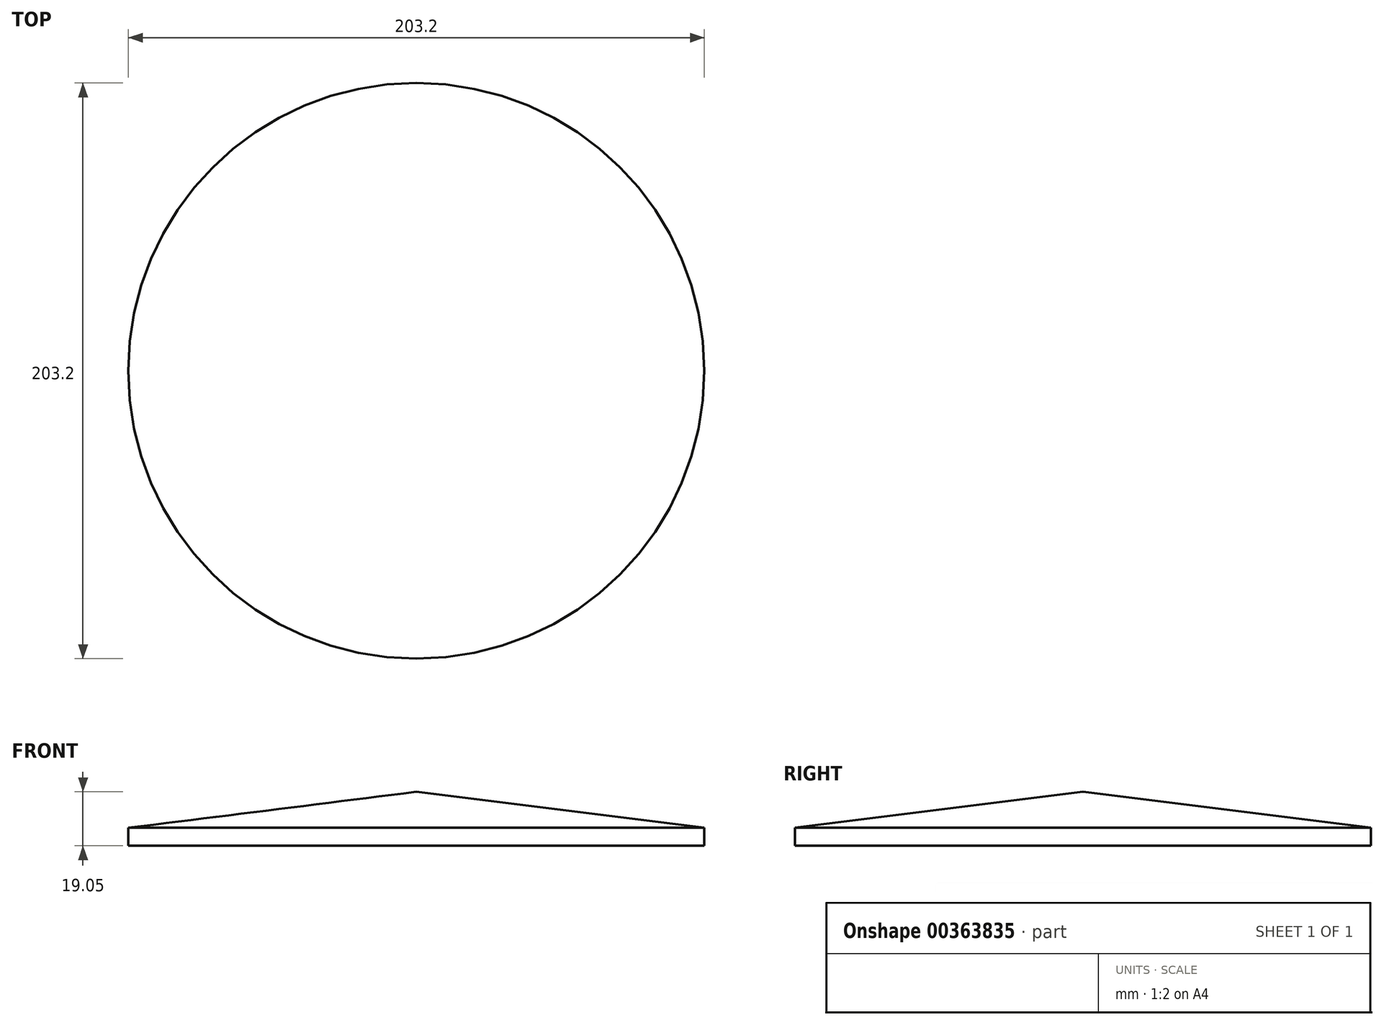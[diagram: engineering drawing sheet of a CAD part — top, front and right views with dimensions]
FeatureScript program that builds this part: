
annotation { "Feature Type Name" : "Feature", "Feature Type Description" : "" }
export const myFeature = defineFeature(function(context is Context, id is Id, definition is map)
    precondition{}
    {
        {
            var Q0;
            Q0=qCreatedBy(makeId("Front.planeOp"),FACE);
            var sketch = newSketch(context, id + "F0", { "sketchPlane" : qUnion([Q0])});
            skLineSegment(sketch, "E0.bottom", {"start": v(0, 0) * mm, "end": v(-101.6, 0) * mm});
            skLineSegment(sketch, "E0.top", {"start": v(0, 19.05) * mm, "end": v(-101.6, 19.05) * mm});
            skLineSegment(sketch, "E0.left", {"start": v(0, 0) * mm, "end": v(0, 19.05) * mm});
            skLineSegment(sketch, "E0.right", {"start": v(-101.6, 0) * mm, "end": v(-101.6, 19.05) * mm});
            skLineSegment(sketch, "E1", {"start": v(-101.6, 6.35) * mm, "end": v(0, 19.05) * mm});
            skLineSegment(sketch, "E2.bottom", {"start": v(0, 0) * mm, "end": v(-22.23, 0) * mm});
            skLineSegment(sketch, "E2.top", {"start": v(0, 152.4) * mm, "end": v(-22.23, 152.4) * mm});
            skLineSegment(sketch, "E2.left", {"start": v(0, 0) * mm, "end": v(0, 152.4) * mm});
            skLineSegment(sketch, "E2.right", {"start": v(-22.23, 0) * mm, "end": v(-22.23, 152.4) * mm});
            skLineSegment(sketch, "E3", {"start": v(0, 19.05) * mm, "end": v(0, 0) * mm});
            skSolve(sketch);
        }
        {
            var Q0;
            {var subQ0=sQuery(id+"F0.wireOp",EDGE,"E0.bottom");Q0=makeQuery(id+"F0.imprint","IMPRINT",FACE,{"disambiguationData":[TD([[makeQuery(id+"F0.imprint","IMPRINT",EDGE,{"derivedFrom":subQ0}),-1.0]])]});}
            var Q1;
            Q1=sQuery(id+"F0.wireOp",EDGE,"E3");
            revolve(context, id + "F1", {"entities" : qUnion([Q0]), "axis" : qUnion([Q1]), "revolveType" : RevolveType.FULL});
        }
    });
